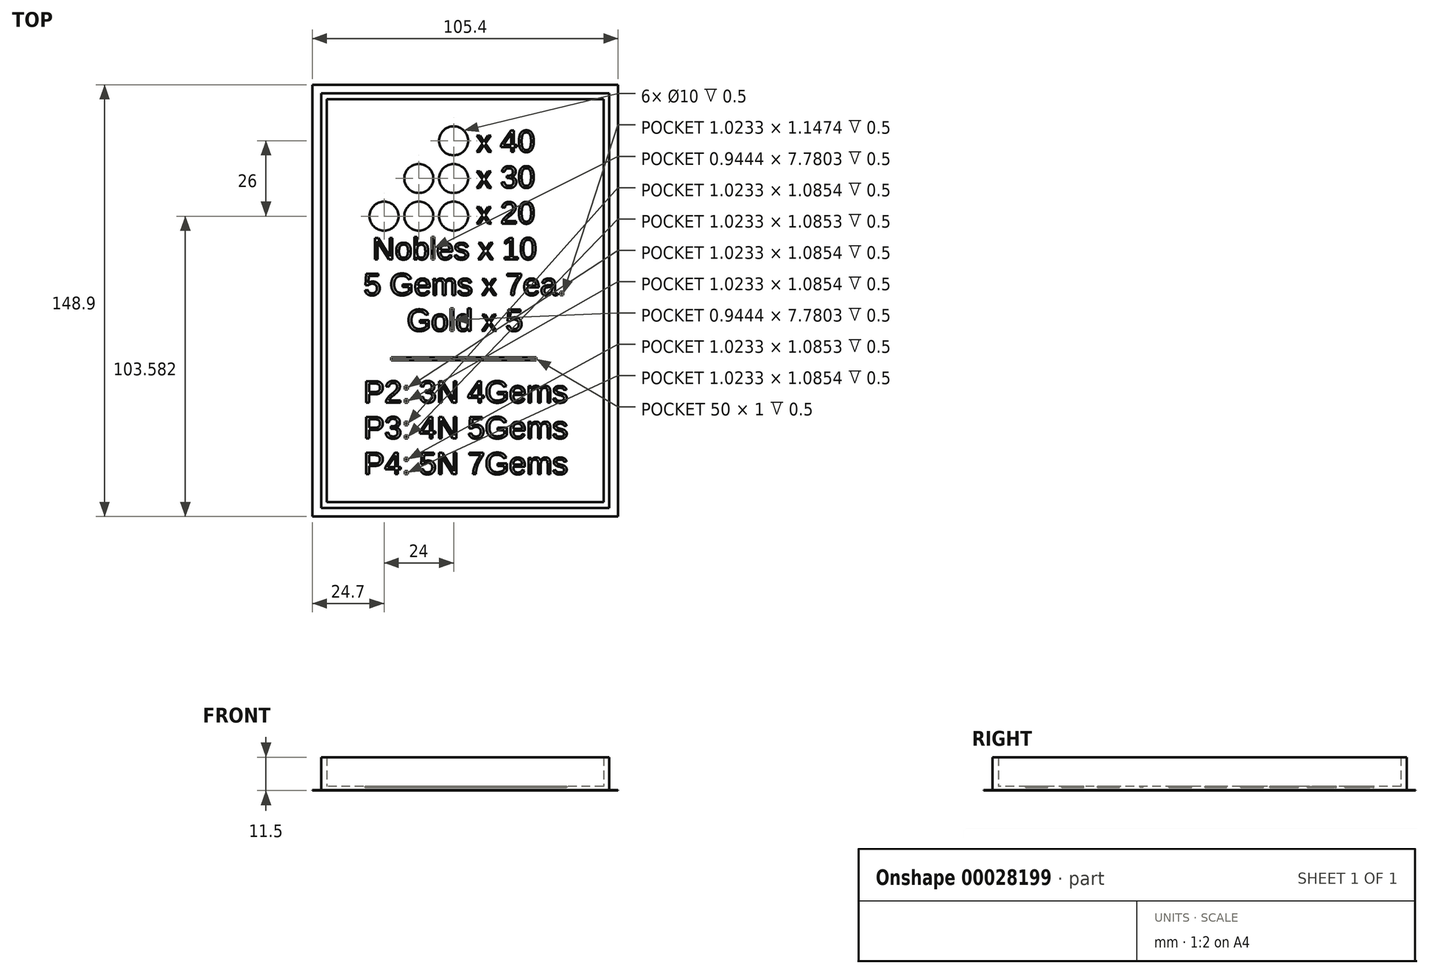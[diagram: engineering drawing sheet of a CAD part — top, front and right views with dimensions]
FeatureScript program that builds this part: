
annotation { "Feature Type Name" : "Feature", "Feature Type Description" : "" }
export const myFeature = defineFeature(function(context is Context, id is Id, definition is map)
    precondition{}
    {
        {
            var Q0;
            Q0=qCreatedBy(makeId("Top.planeOp"),FACE);
            var sketch = newSketch(context, id + "F0", { "sketchPlane" : qUnion([Q0])});
            skLineSegment(sketch, "E0.rect.bottom", {"start": v(49.7, 71.45) * mm, "end": v(-49.7, 71.45) * mm});
            skLineSegment(sketch, "E0.rect.top", {"start": v(49.7, -71.45) * mm, "end": v(-49.7, -71.45) * mm});
            skLineSegment(sketch, "E0.rect.left", {"start": v(49.7, 71.45) * mm, "end": v(49.7, -71.45) * mm});
            skLineSegment(sketch, "E0.rect.right", {"start": v(-49.7, 71.45) * mm, "end": v(-49.7, -71.45) * mm});
            skPoint(sketch, "E0.rect.middle", {"position": v(0, 0) * mm});
            skSolve(sketch);
        }
        {
            var Q0;
            Q0 = qSketchRegion(id + "F0", true);
            extrude(context, id + "F1", {"entities" : qUnion([Q0]), "depth" : 1.5 * mm});
        }
        {
            var Q0;
            Q0=makeQuery(id+"F1.opExtrude","CAP_FACE",FACE,{"disambiguationData":[OSD([sQuery(id+"F0.wireOp",EDGE,"E0.rect.bottom"),sQuery(id+"F0.wireOp",EDGE,"E0.rect.top"),sQuery(id+"F0.wireOp",EDGE,"E0.rect.left"),sQuery(id+"F0.wireOp",EDGE,"E0.rect.right")])],"isStart":false});
            var sketch = newSketch(context, id + "F2", { "sketchPlane" : qUnion([Q0])});
            skLineSegment(sketch, "E1.rect.bottom", {"start": v(49.7, 71.45) * mm, "end": v(-49.7, 71.45) * mm});
            skLineSegment(sketch, "E1.rect.top", {"start": v(49.7, -71.45) * mm, "end": v(-49.7, -71.45) * mm});
            skLineSegment(sketch, "E1.rect.left", {"start": v(49.7, 71.45) * mm, "end": v(49.7, -71.45) * mm});
            skLineSegment(sketch, "E1.rect.right", {"start": v(-49.7, 71.45) * mm, "end": v(-49.7, -71.45) * mm});
            skPoint(sketch, "E1.rect.middle", {"position": v(0, 0) * mm});
            skLineSegment(sketch, "E2.rect.bottom", {"start": v(47.7, 69.45) * mm, "end": v(-47.7, 69.45) * mm});
            skLineSegment(sketch, "E2.rect.top", {"start": v(47.7, -69.45) * mm, "end": v(-47.7, -69.45) * mm});
            skLineSegment(sketch, "E2.rect.left", {"start": v(47.7, 69.45) * mm, "end": v(47.7, -69.45) * mm});
            skLineSegment(sketch, "E2.rect.right", {"start": v(-47.7, 69.45) * mm, "end": v(-47.7, -69.45) * mm});
            skSolve(sketch);
        }
        {
            var Q0;
            Q0 = qSketchRegion(id + "F2", true);
            extrude(context, id + "F3", {"entities" : qUnion([Q0]), "operationType" : NewBodyOperationType.ADD, "depth" : 10 * mm});
        }
        {
            var Q0;
            Q0=makeQuery(id+"F1.opExtrude","CAP_FACE",FACE,{"disambiguationData":[OSD([sQuery(id+"F0.wireOp",EDGE,"E0.rect.bottom"),sQuery(id+"F0.wireOp",EDGE,"E0.rect.top"),sQuery(id+"F0.wireOp",EDGE,"E0.rect.left"),sQuery(id+"F0.wireOp",EDGE,"E0.rect.right")])],"isStart":false});
            var sketch = newSketch(context, id + "F4", { "sketchPlane" : qUnion([Q0])});
            skText(sketch, "E3", { "text": "             x 40\n             x 30\n             x 20\n Nobles x 10\n5 Gems x 7ea.\n     Gold x 5\n\nP2: 3N 4Gems\nP3: 4N 5Gems\nP4: 5N 7Gems", "fontName": "Arimo-Regular.ttf"});
            skLineSegment(sketch, "E4", {"start": v(-35, 55.13) * mm, "end": v(0, 55.13) * mm});
            skLineSegment(sketch, "E5", {"start": v(0, 55.13) * mm, "end": v(-4, 55.13) * mm});
            skLineSegment(sketch, "E6", {"start": v(-4, 55.13) * mm, "end": v(-16, 55.13) * mm});
            skLineSegment(sketch, "E7", {"start": v(-16, 55.13) * mm, "end": v(-28, 55.13) * mm});
            skCircle(sketch, "E8", {"center": v(-4, 55.13) * mm, "radius": 5 * mm});
            skLineSegment(sketch, "E9", {"start": v(-4, 55.13) * mm, "end": v(-4, 42.13) * mm});
            skCircle(sketch, "E10", {"center": v(-4, 42.13) * mm, "radius": 5 * mm});
            skLineSegment(sketch, "E11", {"start": v(-16, 55.13) * mm, "end": v(-16, 29.13) * mm});
            skCircle(sketch, "E12", {"center": v(-16, 42.13) * mm, "radius": 5 * mm});
            skLineSegment(sketch, "E13", {"start": v(-16, 29.13) * mm, "end": v(-4, 29.13) * mm});
            skCircle(sketch, "E14", {"center": v(-4, 29.13) * mm, "radius": 5 * mm});
            skLineSegment(sketch, "E15", {"start": v(-28, 55.13) * mm, "end": v(-28, 29.13) * mm});
            skCircle(sketch, "E16", {"center": v(-16, 29.13) * mm, "radius": 5 * mm});
            skCircle(sketch, "E17", {"center": v(-28, 29.13) * mm, "radius": 5 * mm});
            skPoint(sketch, "E18", {"position": v(-0.49, -20.04) * mm});
            skLineSegment(sketch, "E19.rect.bottom", {"start": v(24.51, -19.54) * mm, "end": v(-25.49, -19.54) * mm});
            skLineSegment(sketch, "E19.rect.top", {"start": v(24.51, -20.54) * mm, "end": v(-25.49, -20.54) * mm});
            skLineSegment(sketch, "E19.rect.left", {"start": v(24.51, -19.54) * mm, "end": v(24.51, -20.54) * mm});
            skLineSegment(sketch, "E19.rect.right", {"start": v(-25.49, -19.54) * mm, "end": v(-25.49, -20.54) * mm});
            const initialGuessF4  = {"E3": [-0.035, 0.05127, 1, 0, 0.00773]};
            skSetInitialGuess(sketch, initialGuessF4);
            skSolve(sketch);
        }
        {
            var Q0;
            Q0 = qSketchRegion(id + "F4", true);
            extrude(context, id + "F5", {"entities" : qUnion([Q0]), "operationType" : NewBodyOperationType.REMOVE, "oppositeDirection" : true, "depth" : .5 * mm});
        }
        {
            var Q0;
            Q0=qCreatedBy(makeId("Top.planeOp"),FACE);
            var sketch = newSketch(context, id + "F6", { "sketchPlane" : qUnion([Q0])});
            skLineSegment(sketch, "E20.0", {"start": v(49.7, -71.45) * mm, "end": v(-49.7, -71.45) * mm});
            skLineSegment(sketch, "E21.0", {"start": v(49.7, 71.45) * mm, "end": v(49.7, -71.45) * mm});
            skLineSegment(sketch, "E22.0", {"start": v(49.7, 71.45) * mm, "end": v(-49.7, 71.45) * mm});
            skLineSegment(sketch, "E23.0", {"start": v(-49.7, 71.45) * mm, "end": v(-49.7, -71.45) * mm});
            skLineSegment(sketch, "E24.0", {"start": v(52.7, 74.45) * mm, "end": v(52.7, -74.45) * mm});
            skLineSegment(sketch, "E24.1", {"start": v(52.7, 74.45) * mm, "end": v(-52.7, 74.45) * mm});
            skLineSegment(sketch, "E24.2", {"start": v(-52.7, 74.45) * mm, "end": v(-52.7, -74.45) * mm});
            skLineSegment(sketch, "E24.3", {"start": v(52.7, -74.45) * mm, "end": v(-52.7, -74.45) * mm});
            skSolve(sketch);
        }
        {
            var Q0;
            Q0 = qSketchRegion(id + "F6", true);
            extrude(context, id + "F7", {"entities" : qUnion([Q0]), "operationType" : NewBodyOperationType.ADD, "depth" : .2 * mm});
        }
    });
